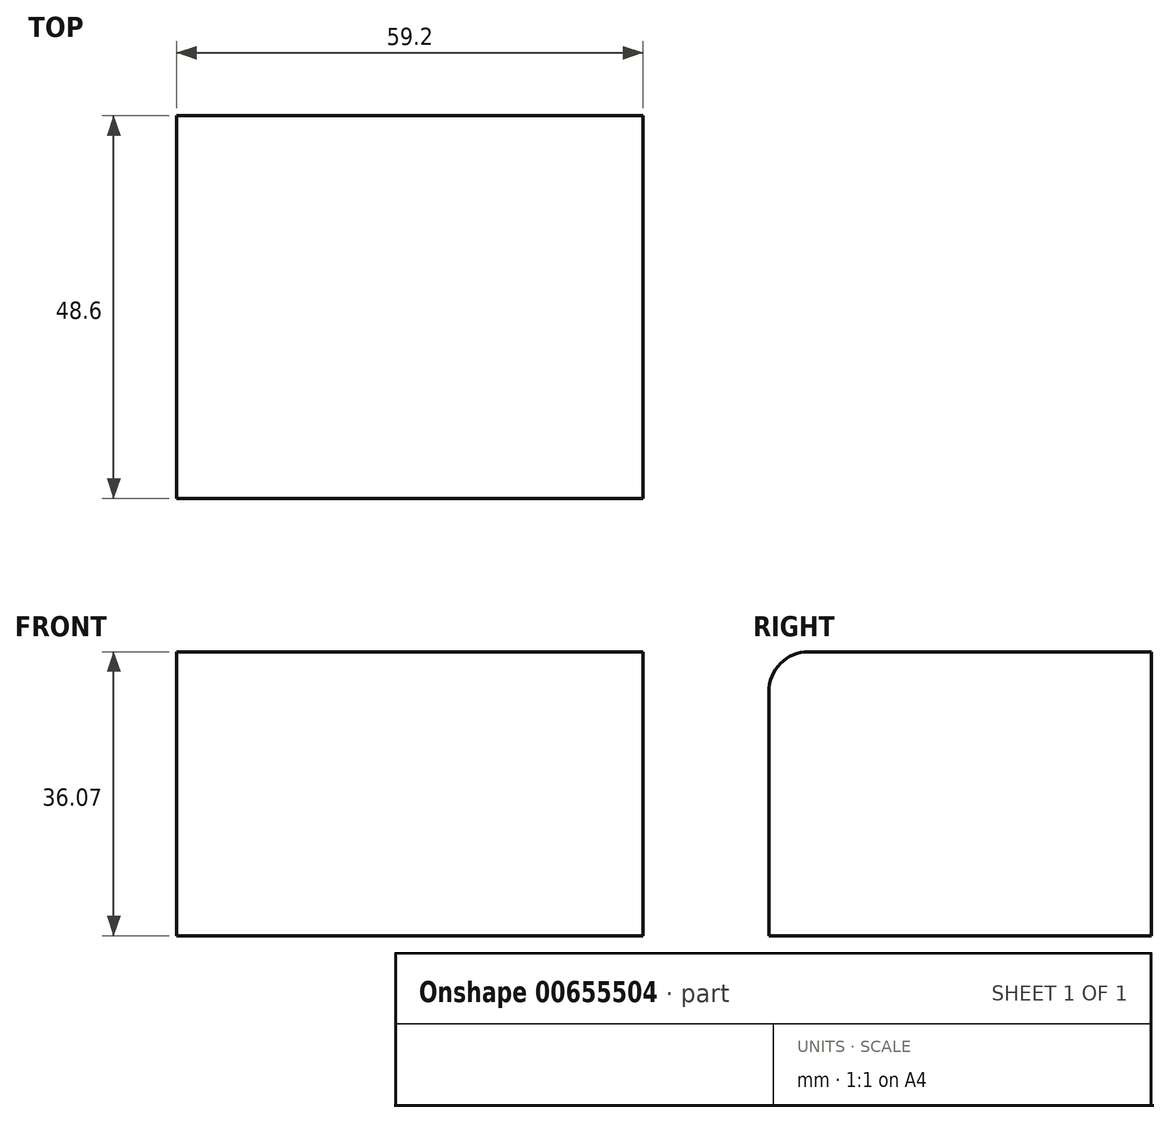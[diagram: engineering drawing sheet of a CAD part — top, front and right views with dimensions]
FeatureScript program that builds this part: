
annotation { "Feature Type Name" : "Feature", "Feature Type Description" : "" }
export const myFeature = defineFeature(function(context is Context, id is Id, definition is map)
    precondition{}
    {
        {
            var Q0;
            Q0=qCreatedBy(makeId("Top.planeOp"),FACE);
            var sketch = newSketch(context, id + "F0", { "sketchPlane" : qUnion([Q0])});
            skLineSegment(sketch, "E0.bottom", {"start": v(-41.8, -24.82) * mm, "end": v(17.4, -24.82) * mm});
            skLineSegment(sketch, "E0.top", {"start": v(-41.8, 23.78) * mm, "end": v(17.4, 23.78) * mm});
            skLineSegment(sketch, "E0.left", {"start": v(-41.8, -24.82) * mm, "end": v(-41.8, 23.78) * mm});
            skLineSegment(sketch, "E0.right", {"start": v(17.4, -24.82) * mm, "end": v(17.4, 23.78) * mm});
            skSolve(sketch);
        }
        {
            var Q0;
            Q0 = qSketchRegion(id + "F0", true);
            extrude(context, id + "F1", {"entities" : qUnion([Q0]), "depth" : 36.07 * mm, "offsetDistance" : 25.4 * mm});
        }
        {
            var Q0;
            Q0=makeQuery(id+"F1.opExtrude","CAP_EDGE",EDGE,{"disambiguationData":[OSD([sQuery(id+"F0.wireOp",EDGE,"E0.bottom")])],"isStart":false});
            fillet(context, id + "F2", {"entities" : qUnion([Q0]), "radius" : 5.08 * mm, "tangentPropagation" : true, "allowEdgeOverflow" : false});
        }
    });
